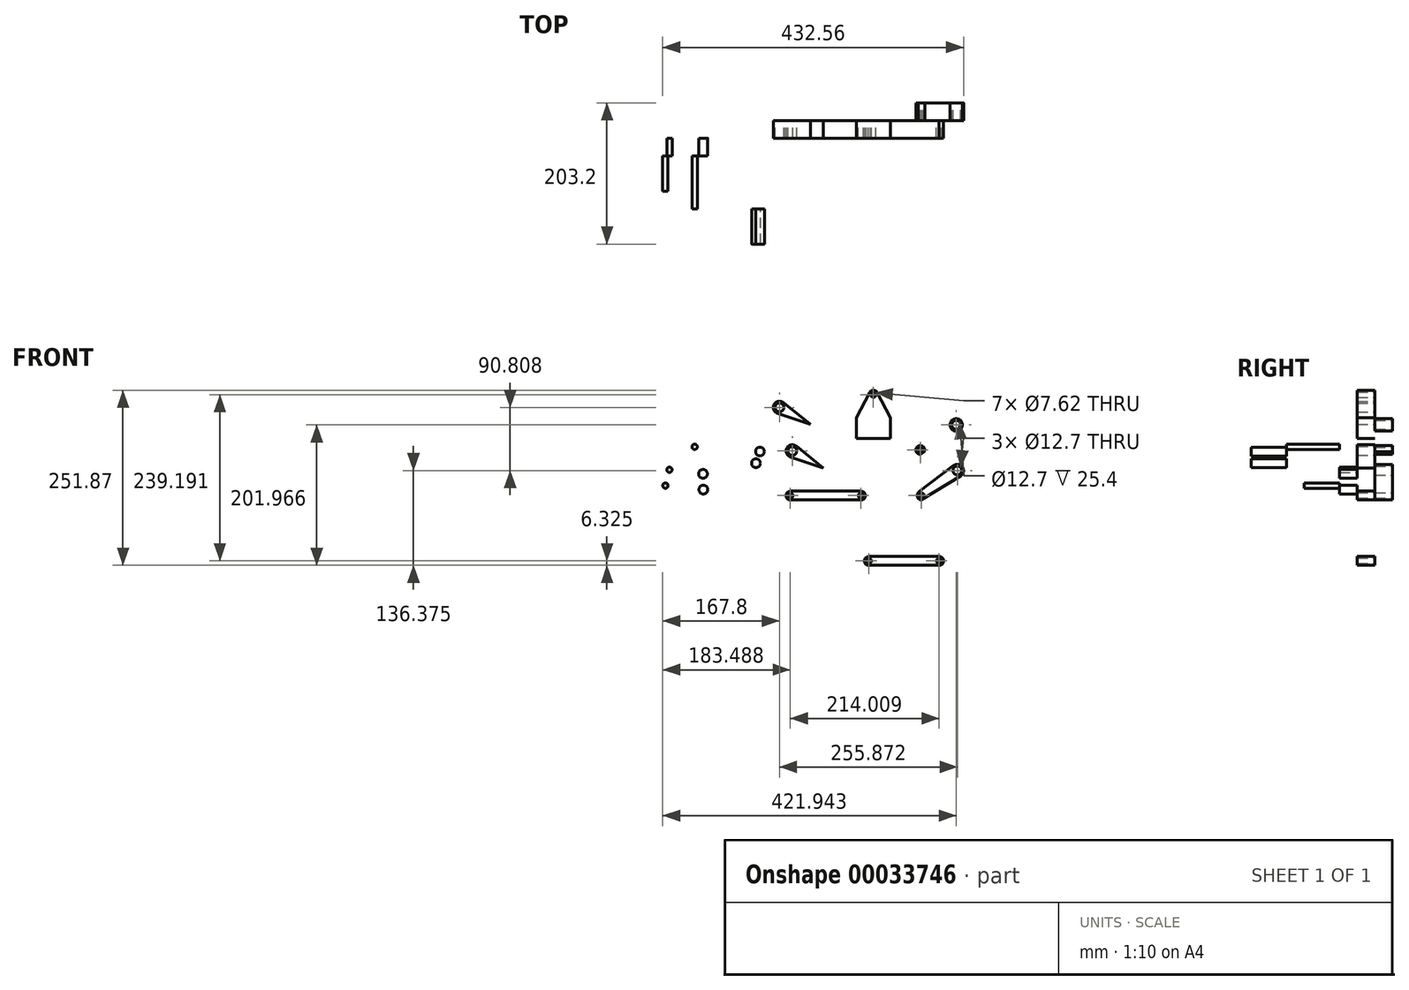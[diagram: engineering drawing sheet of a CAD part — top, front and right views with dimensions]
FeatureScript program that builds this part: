
annotation { "Feature Type Name" : "Feature", "Feature Type Description" : "" }
export const myFeature = defineFeature(function(context is Context, id is Id, definition is map)
    precondition{}
    {
        {
            var Q0;
            Q0=qCreatedBy(makeId("Front.planeOp"),FACE);
            var sketch = newSketch(context, id + "F0", { "sketchPlane" : qUnion([Q0])});
            skLineSegment(sketch, "E0.bottom", {"start": v(-69.08, -26) * mm, "end": v(-43.32, -26) * mm});
            skLineSegment(sketch, "E0.top", {"start": v(-69.08, -13.32) * mm, "end": v(-43.32, -13.32) * mm});
            skLineSegment(sketch, "E0.left", {"start": v(-69.08, -26) * mm, "end": v(-69.08, -13.32) * mm});
            skLineSegment(sketch, "E0.right", {"start": v(-43.32, -26) * mm, "end": v(-43.32, -13.32) * mm});
            skLineSegment(sketch, "E1", {"start": v(-56.2, -26) * mm, "end": v(-56.2, 2.52) * mm});
            skCircle(sketch, "E2", {"center": v(-56.2, 2.52) * mm, "radius": 3.81 * mm});
            skCircle(sketch, "E3", {"center": v(-56.2, 2.52) * mm, "radius": 6.35 * mm});
            skLineSegment(sketch, "E4", {"start": v(-69.08, -13.32) * mm, "end": v(-62.13, 4.8) * mm});
            skLineSegment(sketch, "E5", {"start": v(-43.32, -13.32) * mm, "end": v(-50.27, 4.8) * mm});
            skLineSegment(sketch, "E6", {"start": v(-50.85, -0.9) * mm, "end": v(33.24, 56.12) * mm});
            skLineSegment(sketch, "E7", {"start": v(-57.98, 8.61) * mm, "end": v(26.2, 65.51) * mm});
            skLineSegment(sketch, "E8", {"start": v(26.2, 65.51) * mm, "end": v(33.24, 56.12) * mm});
            skPoint(sketch, "E9", {"position": v(29.72, 60.82) * mm});
            skCircle(sketch, "E10", {"center": v(29.72, 60.82) * mm, "radius": 3.8 * mm});
            skCircle(sketch, "E11", {"center": v(29.72, 60.82) * mm, "radius": 6.35 * mm});
            skLineSegment(sketch, "E12", {"start": v(26.87, 66.5) * mm, "end": v(128.22, 59.3) * mm});
            skLineSegment(sketch, "E13", {"start": v(128.22, 59.3) * mm, "end": v(127.37, 47.37) * mm});
            skLineSegment(sketch, "E14", {"start": v(127.37, 47.37) * mm, "end": v(26.1, 55.6) * mm});
            skCircle(sketch, "E15", {"center": v(127.8, 53.33) * mm, "radius": 3.8 * mm});
            skCircle(sketch, "E16", {"center": v(127.8, 53.33) * mm, "radius": 6.35 * mm});
            skLineSegment(sketch, "E17", {"start": v(127.37, 47.37) * mm, "end": v(134.23, -2.97) * mm});
            skLineSegment(sketch, "E18", {"start": v(128.22, 59.3) * mm, "end": v(169.75, 88.56) * mm});
            skPoint(sketch, "E19", {"position": v(134.14, 53.33) * mm});
            skLineSegment(sketch, "E20", {"start": v(134.14, 53.33) * mm, "end": v(141.36, 3.05) * mm});
            skLineSegment(sketch, "E21", {"start": v(134.14, 53.33) * mm, "end": v(176.58, 81.26) * mm});
            skLineSegment(sketch, "E22", {"start": v(169.75, 88.56) * mm, "end": v(176.58, 81.26) * mm});
            skLineSegment(sketch, "E23", {"start": v(141.36, 3.05) * mm, "end": v(134.23, -2.97) * mm});
            skCircle(sketch, "E24", {"center": v(137.8, 0.04) * mm, "radius": 3.81 * mm});
            skCircle(sketch, "E25", {"center": v(137.8, 0.04) * mm, "radius": 6.35 * mm});
            skCircle(sketch, "E26", {"center": v(173.16, 84.9) * mm, "radius": 3.81 * mm});
            skCircle(sketch, "E27", {"center": v(173.16, 84.9) * mm, "radius": 6.35 * mm});
            skLineSegment(sketch, "E28.bottom", {"start": v(-159.24, 85.18) * mm, "end": v(-110.24, 85.18) * mm});
            skLineSegment(sketch, "E28.top", {"start": v(-159.24, 114.78) * mm, "end": v(-110.24, 114.78) * mm});
            skLineSegment(sketch, "E28.left", {"start": v(-159.24, 85.18) * mm, "end": v(-159.24, 114.78) * mm});
            skLineSegment(sketch, "E28.right", {"start": v(-110.24, 85.18) * mm, "end": v(-110.24, 114.78) * mm});
            skLineSegment(sketch, "E29", {"start": v(-134.74, 85.18) * mm, "end": v(-134.74, 147.96) * mm});
            skCircle(sketch, "E30", {"center": v(-134.74, 147.96) * mm, "radius": 3.8 * mm});
            skCircle(sketch, "E31", {"center": v(-134.74, 147.96) * mm, "radius": 6.35 * mm});
            skLineSegment(sketch, "E32", {"start": v(-159.24, 114.78) * mm, "end": v(-140.37, 150.9) * mm});
            skLineSegment(sketch, "E33", {"start": v(-110.24, 114.78) * mm, "end": v(-129.11, 150.9) * mm});
            skCircle(sketch, "E34", {"center": v(-157.7, -94.47) * mm, "radius": 3.81 * mm});
            skCircle(sketch, "E35", {"center": v(-157.7, -94.47) * mm, "radius": 6.35 * mm});
            skLineSegment(sketch, "E36", {"start": v(-157.72, -100.82) * mm, "end": v(-56.12, -100.82) * mm});
            skLineSegment(sketch, "E37", {"start": v(-157.7, -88.12) * mm, "end": v(-56.1, -88.12) * mm});
            skLineSegment(sketch, "E38", {"start": v(-56.1, -88.12) * mm, "end": v(-56.12, -100.82) * mm});
            skCircle(sketch, "E39", {"center": v(-56.11, -94.47) * mm, "radius": 3.8 * mm});
            skCircle(sketch, "E40", {"center": v(-56.11, -94.47) * mm, "radius": 6.35 * mm});
            skCircle(sketch, "E41", {"center": v(56.3, -188.38) * mm, "radius": 6.35 * mm});
            skCircle(sketch, "E42", {"center": v(-44.94, -188.4) * mm, "radius": 6.35 * mm});
            skLineSegment(sketch, "E43", {"start": v(-45.65, -194.71) * mm, "end": v(55.95, -194.71) * mm});
            skLineSegment(sketch, "E44", {"start": v(-44.94, -182.05) * mm, "end": v(56.66, -182.05) * mm});
            skCircle(sketch, "E45", {"center": v(56.3, -188.38) * mm, "radius": 3.8 * mm});
            skCircle(sketch, "E46", {"center": v(-44.94, -188.4) * mm, "radius": 3.81 * mm});
            skLineSegment(sketch, "E47", {"start": v(56.66, -182.05) * mm, "end": v(55.95, -194.71) * mm});
            skCircle(sketch, "E48", {"center": v(-287.6, 86.88) * mm, "radius": 6.35 * mm});
            skCircle(sketch, "E49", {"center": v(-287.6, 86.88) * mm, "radius": 3.81 * mm});
            skCircle(sketch, "E50", {"center": v(-236, 122.88) * mm, "radius": 6.35 * mm});
            skCircle(sketch, "E51", {"center": v(-236, 122.88) * mm, "radius": 8.89 * mm});
            skLineSegment(sketch, "E52", {"start": v(-287.6, 80.53) * mm, "end": v(-231.33, 115.31) * mm});
            skCircle(sketch, "E53", {"center": v(-234.28, 57.29) * mm, "radius": 8.89 * mm});
            skCircle(sketch, "E54", {"center": v(-234.28, 57.29) * mm, "radius": 6.35 * mm});
            skLineSegment(sketch, "E55", {"start": v(-289.69, 26.36) * mm, "end": v(-234.28, 68.45) * mm});
            skCircle(sketch, "E56", {"center": v(-285.88, 21.29) * mm, "radius": 6.35 * mm});
            skLineSegment(sketch, "E57", {"start": v(-285.88, 14.94) * mm, "end": v(-229.6, 49.72) * mm});
            skCircle(sketch, "E58", {"center": v(-285.88, 21.29) * mm, "radius": 3.81 * mm});
            skCircle(sketch, "E59", {"center": v(-300.8, -25.32) * mm, "radius": 6.35 * mm});
            skCircle(sketch, "E60", {"center": v(-300.8, -25.32) * mm, "radius": 8.9 * mm});
            skLineSegment(sketch, "E61", {"start": v(-256.27, -49.76) * mm, "end": v(-295.23, -18.4) * mm});
            skLineSegment(sketch, "E62", {"start": v(-256.27, -49.76) * mm, "end": v(-303.65, -33.74) * mm});
            skCircle(sketch, "E63", {"center": v(-282.28, -88.01) * mm, "radius": 8.9 * mm});
            skLineSegment(sketch, "E64", {"start": v(-237.74, -112.45) * mm, "end": v(-285.13, -96.44) * mm});
            skLineSegment(sketch, "E65", {"start": v(-237.74, -112.45) * mm, "end": v(-276.7, -81.09) * mm});
            skCircle(sketch, "E66", {"center": v(-282.28, -88.01) * mm, "radius": 6.35 * mm});
            skLineSegment(sketch, "E67", {"start": v(-292, 91.46) * mm, "end": v(-241.39, 129.95) * mm});
            skSolve(sketch);
        }
        {
            var Q0;
            Q0=makeQuery(id+"F0.imprint","IMPRINT",FACE,{"disambiguationData":[TD([[makeQuery(id+"F0.imprint","IMPRINT",EDGE,{"derivedFrom":sQuery(id+"F0.wireOp",EDGE,"E49")}),-1.0]])]});
            var Q1;
            {var subQ0=sQuery(id+"F0.wireOp",EDGE,"E67");var subQ1=sQuery(id+"F0.wireOp",EDGE,"E48");var subQ2=makeQuery(id+"F0.imprint","INTERSECT",VERTEX,{"disambiguationData":[OD(1.0)],"derivedFrom":[subQ1,subQ0]});Q1=makeQuery(id+"F0.imprint","IMPRINT",FACE,{"disambiguationData":[TD([[makeQuery(id+"F0.imprint","IMPRINT",EDGE,{"disambiguationData":[TD([[subQ2,1.0]])],"derivedFrom":subQ1}),-1.0]])]});}
            var Q2;
            Q2=makeQuery(id+"F0.imprint","IMPRINT",FACE,{"disambiguationData":[TD([[makeQuery(id+"F0.imprint","IMPRINT",EDGE,{"derivedFrom":sQuery(id+"F0.wireOp",EDGE,"E50")}),-1.0]])]});
            var Q3;
            {var subQ0=sQuery(id+"F0.wireOp",EDGE,"E57");var subQ3=sQuery(id+"F0.wireOp",EDGE,"E53");var subQ4=makeQuery(id+"F0.imprint","INTERSECT",VERTEX,{"derivedFrom":[subQ3,subQ0]});Q3=makeQuery(id+"F0.imprint","IMPRINT",FACE,{"disambiguationData":[TD([[makeQuery(id+"F0.imprint","IMPRINT",EDGE,{"disambiguationData":[TD([[subQ4,1.0]])],"derivedFrom":subQ3}),-1.0]])]});}
            var Q4;
            Q4=makeQuery(id+"F0.imprint","IMPRINT",FACE,{"disambiguationData":[TD([[makeQuery(id+"F0.imprint","IMPRINT",EDGE,{"derivedFrom":sQuery(id+"F0.wireOp",EDGE,"E58")}),-1.0]])]});
            var Q5;
            Q5=makeQuery(id+"F0.imprint","IMPRINT",FACE,{"disambiguationData":[TD([[makeQuery(id+"F0.imprint","IMPRINT",EDGE,{"derivedFrom":sQuery(id+"F0.wireOp",EDGE,"E54")}),-1.0]])]});
            extrude(context, id + "F1", {"entities" : qUnion([Q0, Q1, Q2, Q3, Q4, Q5]), "depth" : 25.4 * mm});
        }
        {
            var Q0;
            Q0=makeQuery(id+"F1.opExtrude","CAP_FACE",FACE,{"disambiguationData":[OSD([sQuery(id+"F0.wireOp",EDGE,"E53"),sQuery(id+"F0.wireOp",EDGE,"E54"),sQuery(id+"F0.wireOp",EDGE,"E55"),sQuery(id+"F0.wireOp",EDGE,"E56"),sQuery(id+"F0.wireOp",EDGE,"E57"),sQuery(id+"F0.wireOp",EDGE,"E58")])],"isStart":false});
            var sketch = newSketch(context, id + "F2", { "sketchPlane" : qUnion([Q0])});
            skLineSegment(sketch, "E68", {"start": v(-427.1, 60.96) * mm, "end": v(-466.05, 92.32) * mm});
            skCircle(sketch, "E69", {"center": v(-471.63, 85.4) * mm, "radius": 6.35 * mm});
            skLineSegment(sketch, "E70", {"start": v(-445.62, 123.65) * mm, "end": v(-493, 139.67) * mm});
            skCircle(sketch, "E71", {"center": v(-490.15, 148.1) * mm, "radius": 6.35 * mm});
            skLineSegment(sketch, "E72", {"start": v(-427.1, 60.96) * mm, "end": v(-474.47, 76.97) * mm});
            skCircle(sketch, "E73", {"center": v(-490.15, 148.1) * mm, "radius": 8.9 * mm});
            skLineSegment(sketch, "E74", {"start": v(-445.62, 123.65) * mm, "end": v(-484.58, 155.02) * mm});
            skCircle(sketch, "E75", {"center": v(-471.63, 85.4) * mm, "radius": 8.9 * mm});
            skSolve(sketch);
        }
        {
            var Q0;
            {var subQ2=sQuery(id+"F2.wireOp",EDGE,"E70");Q0=makeQuery(id+"F2.imprint","IMPRINT",FACE,{"disambiguationData":[TD([[makeQuery(id+"F2.imprint","IMPRINT",EDGE,{"derivedFrom":subQ2}),-1.0]])]});}
            var Q1;
            Q1=makeQuery(id+"F2.imprint","IMPRINT",FACE,{"disambiguationData":[TD([[makeQuery(id+"F2.imprint","IMPRINT",EDGE,{"derivedFrom":sQuery(id+"F2.wireOp",EDGE,"E71")}),-1.0]])]});
            var Q2;
            Q2=makeQuery(id+"F2.imprint","IMPRINT",FACE,{"disambiguationData":[TD([[makeQuery(id+"F2.imprint","IMPRINT",EDGE,{"derivedFrom":sQuery(id+"F2.wireOp",EDGE,"E69")}),-1.0]])]});
            var Q3;
            {var subQ2=sQuery(id+"F2.wireOp",EDGE,"E68");Q3=makeQuery(id+"F2.imprint","IMPRINT",FACE,{"disambiguationData":[TD([[makeQuery(id+"F2.imprint","IMPRINT",EDGE,{"derivedFrom":subQ2}),1.0]])]});}
            extrude(context, id + "F3", {"entities" : qUnion([Q0, Q1, Q2, Q3]), "depth" : 25.4 * mm});
        }
        {
            var Q0;
            Q0=makeQuery(id+"F1.opExtrude","CAP_FACE",FACE,{"disambiguationData":[OSD([sQuery(id+"F0.wireOp",EDGE,"E53"),sQuery(id+"F0.wireOp",EDGE,"E54"),sQuery(id+"F0.wireOp",EDGE,"E55"),sQuery(id+"F0.wireOp",EDGE,"E56"),sQuery(id+"F0.wireOp",EDGE,"E57"),sQuery(id+"F0.wireOp",EDGE,"E58")])],"isStart":false});
            var sketch = newSketch(context, id + "F4", { "sketchPlane" : qUnion([Q0])});
            skCircle(sketch, "E76", {"center": v(-361.7, -72.77) * mm, "radius": 6.35 * mm});
            skLineSegment(sketch, "E77", {"start": v(-362.41, -79.07) * mm, "end": v(-260.81, -79.07) * mm});
            skCircle(sketch, "E78", {"center": v(-372.87, 21.17) * mm, "radius": 6.35 * mm});
            skCircle(sketch, "E79", {"center": v(-474.46, 21.17) * mm, "radius": 6.35 * mm});
            skCircle(sketch, "E80", {"center": v(-260.45, -72.74) * mm, "radius": 6.35 * mm});
            skLineSegment(sketch, "E81", {"start": v(-361.7, -66.42) * mm, "end": v(-260.1, -66.42) * mm});
            skLineSegment(sketch, "E82", {"start": v(-474.47, 14.82) * mm, "end": v(-372.87, 14.82) * mm});
            skLineSegment(sketch, "E83", {"start": v(-474.46, 27.52) * mm, "end": v(-372.86, 27.52) * mm});
            skCircle(sketch, "E84", {"center": v(-474.46, 21.17) * mm, "radius": 3.81 * mm});
            skLineSegment(sketch, "E85", {"start": v(-260.1, -66.42) * mm, "end": v(-260.81, -79.07) * mm});
            skLineSegment(sketch, "E86", {"start": v(-372.86, 27.52) * mm, "end": v(-372.87, 14.82) * mm});
            skCircle(sketch, "E87", {"center": v(-361.7, -72.77) * mm, "radius": 3.81 * mm});
            skCircle(sketch, "E88", {"center": v(-260.45, -72.74) * mm, "radius": 3.8 * mm});
            skCircle(sketch, "E89", {"center": v(-372.87, 21.17) * mm, "radius": 3.8 * mm});
            skSolve(sketch);
        }
        {
            var Q0;
            {var subQ1=sQuery(id+"F4.wireOp",EDGE,"E82");Q0=makeQuery(id+"F4.imprint","IMPRINT",FACE,{"disambiguationData":[TD([[makeQuery(id+"F4.imprint","IMPRINT",EDGE,{"derivedFrom":subQ1}),1.0]])]});}
            var Q1;
            Q1=makeQuery(id+"F4.imprint","IMPRINT",FACE,{"disambiguationData":[TD([[makeQuery(id+"F4.imprint","IMPRINT",EDGE,{"derivedFrom":sQuery(id+"F4.wireOp",EDGE,"E84")}),-1.0]])]});
            var Q2;
            {var subQ0=sQuery(id+"F4.wireOp",EDGE,"E89");var subQ1=sQuery(id+"F4.wireOp",EDGE,"E86");var subQ3=makeQuery(id+"F4.imprint","INTERSECT",VERTEX,{"disambiguationData":[OD(0.0)],"derivedFrom":[subQ1,subQ0]});Q2=makeQuery(id+"F4.imprint","IMPRINT",FACE,{"disambiguationData":[TD([[makeQuery(id+"F4.imprint","IMPRINT",EDGE,{"disambiguationData":[TD([[subQ3,-1.0]])],"derivedFrom":subQ0}),-1.0]])]});}
            var Q3;
            {var subQ0=sQuery(id+"F4.wireOp",EDGE,"E89");var subQ1=sQuery(id+"F4.wireOp",EDGE,"E86");var subQ3=makeQuery(id+"F4.imprint","INTERSECT",VERTEX,{"disambiguationData":[OD(0.0)],"derivedFrom":[subQ1,subQ0]});Q3=makeQuery(id+"F4.imprint","IMPRINT",FACE,{"disambiguationData":[TD([[makeQuery(id+"F4.imprint","IMPRINT",EDGE,{"disambiguationData":[TD([[subQ3,1.0]])],"derivedFrom":subQ0}),-1.0]])]});}
            var Q4;
            {var subQ0=sQuery(id+"F4.wireOp",EDGE,"E81");var subQ3=sQuery(id+"F4.wireOp",EDGE,"E76");var subQ4=makeQuery(id+"F4.imprint","INTERSECT",VERTEX,{"derivedFrom":[subQ3,subQ0]});Q4=makeQuery(id+"F4.imprint","IMPRINT",FACE,{"disambiguationData":[TD([[makeQuery(id+"F4.imprint","IMPRINT",EDGE,{"disambiguationData":[TD([[subQ4,1.0]])],"derivedFrom":subQ3}),-1.0]])]});}
            var Q5;
            Q5=makeQuery(id+"F4.imprint","IMPRINT",FACE,{"disambiguationData":[TD([[makeQuery(id+"F4.imprint","IMPRINT",EDGE,{"derivedFrom":sQuery(id+"F4.wireOp",EDGE,"E87")}),-1.0]])]});
            var Q6;
            {var subQ1=sQuery(id+"F4.wireOp",EDGE,"E85");var subQ4=sQuery(id+"F4.wireOp",EDGE,"E77");var subQ5=makeQuery(id+"F4.imprint","INTERSECT",VERTEX,{"derivedFrom":[subQ4,subQ1]});Q6=makeQuery(id+"F4.imprint","IMPRINT",FACE,{"disambiguationData":[TD([[makeQuery(id+"F4.imprint","IMPRINT",EDGE,{"disambiguationData":[TD([[subQ5,1.0]])],"derivedFrom":subQ4}),1.0]])]});}
            var Q7;
            {var subQ1=sQuery(id+"F4.wireOp",EDGE,"E85");var subQ4=sQuery(id+"F4.wireOp",EDGE,"E77");var subQ5=makeQuery(id+"F4.imprint","INTERSECT",VERTEX,{"derivedFrom":[subQ4,subQ1]});Q7=makeQuery(id+"F4.imprint","IMPRINT",FACE,{"disambiguationData":[TD([[makeQuery(id+"F4.imprint","IMPRINT",EDGE,{"disambiguationData":[TD([[subQ5,1.0]])],"derivedFrom":subQ4}),-1.0]])]});}
            extrude(context, id + "F5", {"entities" : qUnion([Q0, Q1, Q2, Q3, Q4, Q5, Q6, Q7]), "depth" : 25.4 * mm});
        }
        {
            var Q0;
            Q0=makeQuery(id+"F1.opExtrude","CAP_FACE",FACE,{"disambiguationData":[OSD([sQuery(id+"F0.wireOp",EDGE,"E53"),sQuery(id+"F0.wireOp",EDGE,"E54"),sQuery(id+"F0.wireOp",EDGE,"E55"),sQuery(id+"F0.wireOp",EDGE,"E56"),sQuery(id+"F0.wireOp",EDGE,"E57"),sQuery(id+"F0.wireOp",EDGE,"E58")])],"isStart":false});
            var sketch = newSketch(context, id + "F6", { "sketchPlane" : qUnion([Q0])});
            skLineSegment(sketch, "E90.left", {"start": v(-379.59, 103.65) * mm, "end": v(-379.59, 133.25) * mm});
            skLineSegment(sketch, "E91", {"start": v(-330.59, 133.25) * mm, "end": v(-349.46, 169.37) * mm});
            skLineSegment(sketch, "E90.top", {"start": v(-379.59, 133.25) * mm, "end": v(-330.59, 133.25) * mm});
            skLineSegment(sketch, "E90.bottom", {"start": v(-379.59, 103.65) * mm, "end": v(-330.59, 103.65) * mm});
            skLineSegment(sketch, "E92", {"start": v(-379.59, 133.25) * mm, "end": v(-360.71, 169.37) * mm});
            skLineSegment(sketch, "E90.right", {"start": v(-330.59, 103.65) * mm, "end": v(-330.59, 133.25) * mm});
            skCircle(sketch, "E93", {"center": v(-355.09, 166.43) * mm, "radius": 6.35 * mm});
            skLineSegment(sketch, "E94", {"start": v(-355.09, 103.65) * mm, "end": v(-355.09, 166.43) * mm});
            skCircle(sketch, "E95", {"center": v(-355.09, 166.43) * mm, "radius": 3.8 * mm});
            skSolve(sketch);
        }
        {
            var Q0;
            {var subQ5=sQuery(id+"F6.wireOp",EDGE,"E90.left");Q0=makeQuery(id+"F6.imprint","IMPRINT",FACE,{"disambiguationData":[TD([[makeQuery(id+"F6.imprint","IMPRINT",EDGE,{"derivedFrom":subQ5}),-1.0]])]});}
            var sketch = newSketch(context, id + "F7", { "sketchPlane" : qUnion([Q0])});
            skSolve(sketch);
        }
        {
            var Q0;
            Q0 = qSketchRegion(id + "F7", true);
            var Q1;
            {var subQ5=sQuery(id+"F6.wireOp",EDGE,"E90.left");Q1=makeQuery(id+"F6.imprint","IMPRINT",FACE,{"disambiguationData":[TD([[makeQuery(id+"F6.imprint","IMPRINT",EDGE,{"derivedFrom":subQ5}),-1.0]])]});}
            var Q2;
            {var subQ5=sQuery(id+"F6.wireOp",EDGE,"E90.right");Q2=makeQuery(id+"F6.imprint","IMPRINT",FACE,{"disambiguationData":[TD([[makeQuery(id+"F6.imprint","IMPRINT",EDGE,{"derivedFrom":subQ5}),1.0]])]});}
            var Q3;
            {var subQ5=sQuery(id+"F6.wireOp",EDGE,"E92");Q3=makeQuery(id+"F6.imprint","IMPRINT",FACE,{"disambiguationData":[TD([[makeQuery(id+"F6.imprint","IMPRINT",EDGE,{"derivedFrom":subQ5}),-1.0]])]});}
            var Q4;
            {var subQ5=sQuery(id+"F6.wireOp",EDGE,"E91");Q4=makeQuery(id+"F6.imprint","IMPRINT",FACE,{"disambiguationData":[TD([[makeQuery(id+"F6.imprint","IMPRINT",EDGE,{"derivedFrom":subQ5}),1.0]])]});}
            var Q5;
            Q5=makeQuery(id+"F6.imprint","IMPRINT",FACE,{"disambiguationData":[TD([[makeQuery(id+"F6.imprint","IMPRINT",EDGE,{"derivedFrom":sQuery(id+"F6.wireOp",EDGE,"E95")}),-1.0]])]});
            extrude(context, id + "F8", {"entities" : qUnion([Q0, Q1, Q2, Q3, Q4, Q5]), "depth" : 25.4 * mm});
        }
        {
            var Q0;
            Q0=makeQuery(id+"F5.opExtrude","CAP_FACE",FACE,{"disambiguationData":[OSD([sQuery(id+"F4.wireOp",EDGE,"E78"),sQuery(id+"F4.wireOp",EDGE,"E79"),sQuery(id+"F4.wireOp",EDGE,"E82"),sQuery(id+"F4.wireOp",EDGE,"E83"),sQuery(id+"F4.wireOp",EDGE,"E84"),sQuery(id+"F4.wireOp",EDGE,"E89")])],"isStart":false});
            var sketch = newSketch(context, id + "F9", { "sketchPlane" : qUnion([Q0])});
            skCircle(sketch, "E96", {"center": v(-627.3, 48.56) * mm, "radius": 3.81 * mm});
            skCircle(sketch, "E97", {"center": v(-600.09, 52.5) * mm, "radius": 6.35 * mm});
            skCircle(sketch, "E98", {"center": v(-599.6, 29.85) * mm, "radius": 6.35 * mm});
            skCircle(sketch, "E99", {"center": v(-652.29, 18.52) * mm, "radius": 3.81 * mm});
            skCircle(sketch, "E100", {"center": v(-648.35, 58.41) * mm, "radius": 3.81 * mm});
            skSolve(sketch);
        }
        {
            var Q0;
            Q0=makeQuery(id+"F9.imprint","IMPRINT",FACE,{"disambiguationData":[TD([[makeQuery(id+"F9.imprint","IMPRINT",EDGE,{"derivedFrom":sQuery(id+"F9.wireOp",EDGE,"E97")}),1.0]])]});
            var Q1;
            Q1=makeQuery(id+"F9.imprint","IMPRINT",FACE,{"disambiguationData":[TD([[makeQuery(id+"F9.imprint","IMPRINT",EDGE,{"derivedFrom":sQuery(id+"F9.wireOp",EDGE,"E98")}),1.0]])]});
            var Q2;
            Q2=makeQuery(id+"F9.imprint","IMPRINT",FACE,{"disambiguationData":[TD([[makeQuery(id+"F9.imprint","IMPRINT",EDGE,{"derivedFrom":sQuery(id+"F9.wireOp",EDGE,"E100")}),1.0]])]});
            extrude(context, id + "F10", {"entities" : qUnion([Q0, Q1, Q2]), "depth" : 25.4 * mm});
        }
        {
            var Q0;
            Q0=makeQuery(id+"F10.opExtrude","CAP_FACE",FACE,{"disambiguationData":[OSD([sQuery(id+"F9.wireOp",EDGE,"E98")])],"isStart":false});
            var sketch = newSketch(context, id + "F11", { "sketchPlane" : qUnion([Q0])});
            skCircle(sketch, "E101", {"center": v(-654.14, 35.6) * mm, "radius": 3.81 * mm});
            skSolve(sketch);
        }
        {
            var Q0;
            Q0=makeQuery(id+"F11.imprint","IMPRINT",FACE,{"disambiguationData":[TD([[makeQuery(id+"F11.imprint","IMPRINT",EDGE,{"derivedFrom":sQuery(id+"F11.wireOp",EDGE,"E101")}),1.0]])]});
            extrude(context, id + "F12", {"entities" : qUnion([Q0]), "depth" : 50.8 * mm});
        }
        {
            var Q0;
            Q0=makeQuery(id+"F10.opExtrude","CAP_FACE",FACE,{"disambiguationData":[OSD([sQuery(id+"F9.wireOp",EDGE,"E97")])],"isStart":false});
            var sketch = newSketch(context, id + "F13", { "sketchPlane" : qUnion([Q0])});
            skCircle(sketch, "E102", {"center": v(-612.06, 91.4) * mm, "radius": 3.81 * mm});
            skCircle(sketch, "E103", {"center": v(-612.06, 91.4) * mm, "radius": 6.35 * mm});
            skSolve(sketch);
        }
        {
            var Q0;
            Q0=makeQuery(id+"F13.imprint","IMPRINT",FACE,{"disambiguationData":[TD([[makeQuery(id+"F13.imprint","IMPRINT",EDGE,{"derivedFrom":sQuery(id+"F13.wireOp",EDGE,"E102")}),1.0]])]});
            extrude(context, id + "F14", {"entities" : qUnion([Q0]), "depth" : 76.2 * mm});
        }
        {
            var Q0;
            Q0=makeQuery(id+"F14.opExtrude","CAP_FACE",FACE,{"disambiguationData":[OSD([sQuery(id+"F13.wireOp",EDGE,"E102")])],"isStart":false});
            var sketch = newSketch(context, id + "F15", { "sketchPlane" : qUnion([Q0])});
            skCircle(sketch, "E104", {"center": v(-518.2, 84.65) * mm, "radius": 6.35 * mm});
            skCircle(sketch, "E105", {"center": v(-523.94, 67.87) * mm, "radius": 6.35 * mm});
            skSolve(sketch);
        }
        {
            var Q0;
            Q0=makeQuery(id+"F15.imprint","IMPRINT",FACE,{"disambiguationData":[TD([[makeQuery(id+"F15.imprint","IMPRINT",EDGE,{"derivedFrom":sQuery(id+"F15.wireOp",EDGE,"E104")}),1.0]])]});
            var Q1;
            Q1=makeQuery(id+"F15.imprint","IMPRINT",FACE,{"disambiguationData":[TD([[makeQuery(id+"F15.imprint","IMPRINT",EDGE,{"derivedFrom":sQuery(id+"F15.wireOp",EDGE,"E105")}),1.0]])]});
            extrude(context, id + "F16", {"entities" : qUnion([Q0, Q1]), "depth" : 50.8 * mm});
        }
    });
